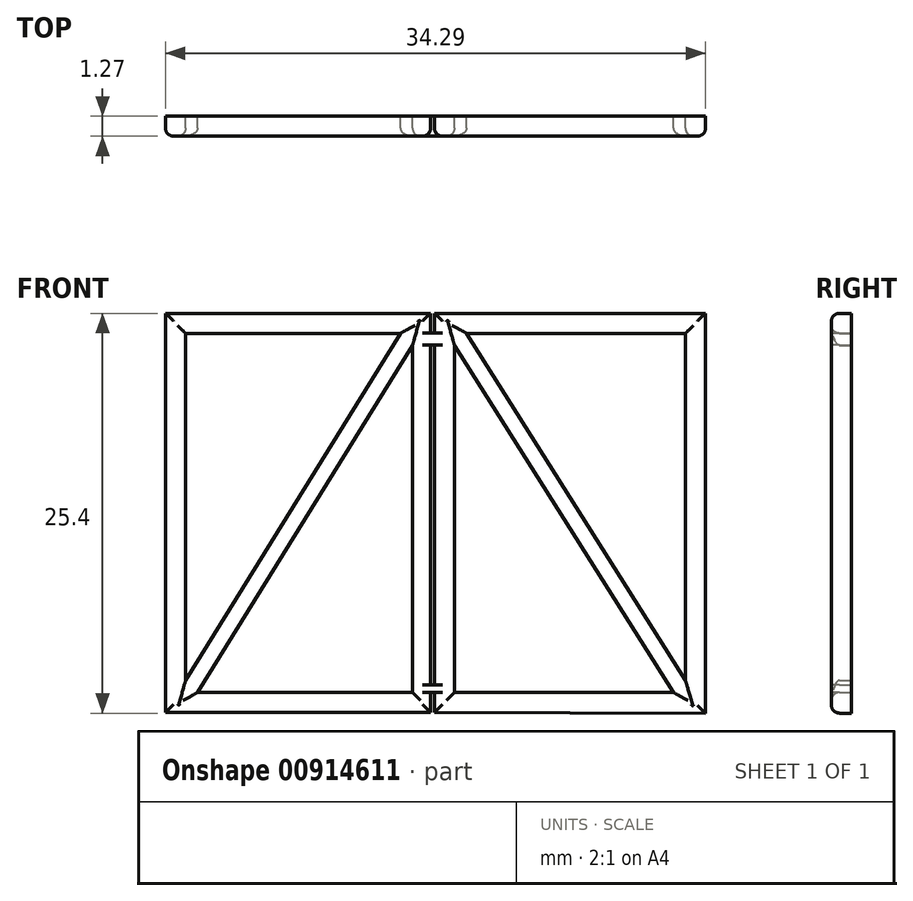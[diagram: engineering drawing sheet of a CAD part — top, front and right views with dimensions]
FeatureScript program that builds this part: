
annotation { "Feature Type Name" : "Feature", "Feature Type Description" : "" }
export const myFeature = defineFeature(function(context is Context, id is Id, definition is map)
    precondition{}
    {
        {
            var Q0;
            Q0=qCreatedBy(makeId("Front.planeOp"),FACE);
            var sketch = newSketch(context, id + "F0", { "sketchPlane" : qUnion([Q0])});
            skLineSegment(sketch, "E0", {"start": v(98.35, 38.1) * mm, "end": v(97.08, 38.1) * mm, "construction": true});
            skLineSegment(sketch, "E1", {"start": v(97.08, 38.1) * mm, "end": v(97.08, 35.56) * mm, "construction": true});
            skLineSegment(sketch, "E2", {"start": v(97.08, 35.56) * mm, "end": v(62.8, 35.56) * mm, "construction": true});
            skLineSegment(sketch, "E3", {"start": v(97.08, 7.62) * mm, "end": v(62.8, 7.62) * mm});
            skLineSegment(sketch, "E4", {"start": v(97.08, 8.9) * mm, "end": v(97.08, 34.3) * mm});
            skLineSegment(sketch, "E5", {"start": v(97.08, 0) * mm, "end": v(97.08, 6.35) * mm});
            skLineSegment(sketch, "E6", {"start": v(97.08, 6.35) * mm, "end": v(96.57, 6.35) * mm});
            skLineSegment(sketch, "E7", {"start": v(96.57, 6.35) * mm, "end": v(97.08, 6.91) * mm});
            skLineSegment(sketch, "E8", {"start": v(97.08, 6.91) * mm, "end": v(97.08, 7.62) * mm});
            skLineSegment(sketch, "E9.1.0.0", {"start": v(27.23, 8.9) * mm, "end": v(61.52, 8.9) * mm});
            skLineSegment(sketch, "E9.1.0.1", {"start": v(61.52, 7.62) * mm, "end": v(27.23, 7.62) * mm});
            skLineSegment(sketch, "E9.1.0.3", {"start": v(61.52, 0) * mm, "end": v(61.52, 6.35) * mm});
            skLineSegment(sketch, "E9.1.0.5", {"start": v(61.52, 8.9) * mm, "end": v(61.52, 34.3) * mm, "construction": true});
            skLineSegment(sketch, "E9.1.0.6", {"start": v(61.52, 35.56) * mm, "end": v(27.23, 35.56) * mm, "construction": true});
            skLineSegment(sketch, "E9.1.0.7", {"start": v(61.52, 38.1) * mm, "end": v(61.52, 35.56) * mm, "construction": true});
            skLineSegment(sketch, "E9.1.0.8", {"start": v(27.23, 34.3) * mm, "end": v(61.52, 34.3) * mm, "construction": true});
            skLineSegment(sketch, "E9.1.0.9", {"start": v(61.52, 6.35) * mm, "end": v(61.01, 6.35) * mm});
            skLineSegment(sketch, "E9.1.0.10", {"start": v(61.01, 6.35) * mm, "end": v(61.52, 6.91) * mm});
            skLineSegment(sketch, "E9.1.0.11", {"start": v(62.8, 38.1) * mm, "end": v(61.52, 38.1) * mm, "construction": true});
            skLineSegment(sketch, "E9.1.0.14", {"start": v(61.52, 6.91) * mm, "end": v(61.52, 7.62) * mm});
            skLineSegment(sketch, "E9.direction1", {"start": v(62.8, 7.62) * mm, "end": v(27.23, 7.62) * mm, "construction": true});
            skLineSegment(sketch, "E10", {"start": v(64.06, 10.22) * mm, "end": v(78.47, 10.22) * mm});
            skLineSegment(sketch, "E11", {"start": v(78.47, 33.02) * mm, "end": v(78.47, 10.22) * mm});
            skLineSegment(sketch, "E12", {"start": v(62.8, 8.95) * mm, "end": v(62.8, 34.3) * mm});
            skLineSegment(sketch, "E13", {"start": v(64.06, 10.22) * mm, "end": v(64.06, 33.02) * mm});
            skLineSegment(sketch, "E14", {"start": v(64.06, 33.02) * mm, "end": v(78.47, 33.02) * mm});
            skLineSegment(sketch, "E15", {"start": v(64.06, 10.22) * mm, "end": v(64.06, 10.98) * mm});
            skLineSegment(sketch, "E16", {"start": v(78.47, 33.02) * mm, "end": v(77.71, 33.02) * mm});
            skLineSegment(sketch, "E17", {"start": v(77.71, 33.02) * mm, "end": v(64.06, 10.98) * mm});
            skLineSegment(sketch, "E18", {"start": v(64.06, 10.22) * mm, "end": v(64.82, 10.22) * mm});
            skLineSegment(sketch, "E19", {"start": v(78.47, 33.02) * mm, "end": v(78.47, 32.26) * mm});
            skLineSegment(sketch, "E20", {"start": v(78.47, 32.26) * mm, "end": v(64.82, 10.22) * mm});
            skLineSegment(sketch, "E21", {"start": v(62.8, 8.95) * mm, "end": v(79.62, 8.95) * mm});
            skLineSegment(sketch, "E22", {"start": v(79.62, 34.3) * mm, "end": v(62.8, 34.3) * mm});
            skLineSegment(sketch, "E23", {"start": v(79.87, 8.95) * mm, "end": v(97.08, 8.9) * mm});
            skLineSegment(sketch, "E24", {"start": v(79.87, 34.3) * mm, "end": v(97.08, 34.3) * mm});
            skLineSegment(sketch, "E25", {"start": v(95.81, 33.02) * mm, "end": v(95.81, 10.22) * mm});
            skLineSegment(sketch, "E26", {"start": v(81.14, 10.22) * mm, "end": v(81.14, 33.02) * mm});
            skLineSegment(sketch, "E27", {"start": v(81.14, 33.02) * mm, "end": v(95.81, 33.02) * mm});
            skLineSegment(sketch, "E28", {"start": v(81.14, 10.22) * mm, "end": v(95.81, 10.22) * mm});
            skLineSegment(sketch, "E29", {"start": v(95.81, 10.22) * mm, "end": v(95.05, 10.22) * mm});
            skLineSegment(sketch, "E30", {"start": v(95.05, 10.22) * mm, "end": v(81.14, 32.26) * mm});
            skLineSegment(sketch, "E31", {"start": v(81.14, 33.02) * mm, "end": v(81.9, 33.02) * mm});
            skLineSegment(sketch, "E32", {"start": v(81.9, 33.02) * mm, "end": v(95.81, 10.98) * mm});
            skLineSegment(sketch, "E33", {"start": v(79.62, 33.03) * mm, "end": v(79.87, 33.03) * mm});
            skLineSegment(sketch, "E34", {"start": v(79.62, 32.27) * mm, "end": v(79.87, 32.27) * mm});
            skLineSegment(sketch, "E35", {"start": v(79.62, 10.22) * mm, "end": v(79.87, 10.22) * mm});
            skLineSegment(sketch, "E36", {"start": v(79.87, 10.7) * mm, "end": v(79.62, 10.7) * mm});
            skLineSegment(sketch, "E37", {"start": v(79.62, 10.22) * mm, "end": v(79.62, 8.95) * mm});
            skLineSegment(sketch, "E38", {"start": v(79.87, 10.22) * mm, "end": v(79.87, 8.95) * mm});
            skLineSegment(sketch, "E39", {"start": v(79.62, 10.7) * mm, "end": v(79.62, 32.27) * mm});
            skLineSegment(sketch, "E40", {"start": v(79.62, 33.03) * mm, "end": v(79.62, 34.3) * mm});
            skLineSegment(sketch, "E41", {"start": v(79.87, 34.3) * mm, "end": v(79.87, 33.03) * mm});
            skLineSegment(sketch, "E42", {"start": v(79.87, 32.27) * mm, "end": v(79.87, 10.7) * mm});
            skSolve(sketch);
        }
        {
            var Q0;
            Q0=makeQuery(id+"F0.imprint","IMPRINT",FACE,{"disambiguationData":[TD([[makeQuery(id+"F0.imprint","IMPRINT",EDGE,{"derivedFrom":sQuery(id+"F0.wireOp",EDGE,"E4")}),1.0]])]});
            var Q1;
            {var subQ3=sQuery(id+"F0.wireOp",EDGE,"E17");Q1=makeQuery(id+"F0.imprint","IMPRINT",FACE,{"disambiguationData":[TD([[makeQuery(id+"F0.imprint","IMPRINT",EDGE,{"derivedFrom":subQ3}),1.0]])]});}
            var Q2;
            {var subQ3=sQuery(id+"F0.wireOp",EDGE,"E30");Q2=makeQuery(id+"F0.imprint","IMPRINT",FACE,{"disambiguationData":[TD([[makeQuery(id+"F0.imprint","IMPRINT",EDGE,{"derivedFrom":subQ3}),-1.0]])]});}
            extrude(context, id + "F1", {"entities" : qUnion([Q0, Q1, Q2]), "depth" : 1.27 * mm, "offsetDistance" : 25.4 * mm});
        }
        {
            var Q0;
            Q0=makeQuery(id+"F1.opExtrude","CAP_EDGE",EDGE,{"disambiguationData":[OSD([sQuery(id+"F0.wireOp",EDGE,"E22")])],"isStart":false});
            var Q1;
            Q1=makeQuery(id+"F1.opExtrude","CAP_EDGE",EDGE,{"disambiguationData":[OSD([sQuery(id+"F0.wireOp",EDGE,"E14")])],"isStart":false});
            var Q2;
            Q2=makeQuery(id+"F1.opExtrude","CAP_EDGE",EDGE,{"disambiguationData":[OSD([sQuery(id+"F0.wireOp",EDGE,"E17")])],"isStart":false});
            var Q3;
            Q3=makeQuery(id+"F1.opExtrude","CAP_EDGE",EDGE,{"disambiguationData":[OSD([sQuery(id+"F0.wireOp",EDGE,"E20")])],"isStart":false});
            var Q4;
            Q4=makeQuery(id+"F1.opExtrude","CAP_EDGE",EDGE,{"disambiguationData":[OSD([sQuery(id+"F0.wireOp",EDGE,"E11")])],"isStart":false});
            var Q5;
            Q5=makeQuery(id+"F1.opExtrude","CAP_EDGE",EDGE,{"disambiguationData":[OSD([sQuery(id+"F0.wireOp",EDGE,"E39")])],"isStart":false});
            var Q6;
            Q6=makeQuery(id+"F1.opExtrude","CAP_EDGE",EDGE,{"disambiguationData":[OSD([sQuery(id+"F0.wireOp",EDGE,"E40")])],"isStart":false});
            var Q7;
            Q7=makeQuery(id+"F1.opExtrude","CAP_EDGE",EDGE,{"disambiguationData":[OSD([sQuery(id+"F0.wireOp",EDGE,"E41")])],"isStart":false});
            var Q8;
            Q8=makeQuery(id+"F1.opExtrude","CAP_EDGE",EDGE,{"disambiguationData":[OSD([sQuery(id+"F0.wireOp",EDGE,"E24")])],"isStart":false});
            var Q9;
            Q9=makeQuery(id+"F1.opExtrude","CAP_EDGE",EDGE,{"disambiguationData":[OSD([sQuery(id+"F0.wireOp",EDGE,"E26")])],"isStart":false});
            var Q10;
            Q10=makeQuery(id+"F1.opExtrude","CAP_EDGE",EDGE,{"disambiguationData":[OSD([sQuery(id+"F0.wireOp",EDGE,"E30")])],"isStart":false});
            var Q11;
            Q11=makeQuery(id+"F1.opExtrude","CAP_EDGE",EDGE,{"disambiguationData":[OSD([sQuery(id+"F0.wireOp",EDGE,"E27")])],"isStart":false});
            var Q12;
            Q12=makeQuery(id+"F1.opExtrude","CAP_EDGE",EDGE,{"disambiguationData":[OSD([sQuery(id+"F0.wireOp",EDGE,"E4")])],"isStart":false});
            var Q13;
            Q13=makeQuery(id+"F1.opExtrude","CAP_EDGE",EDGE,{"disambiguationData":[OSD([sQuery(id+"F0.wireOp",EDGE,"E25")])],"isStart":false});
            var Q14;
            Q14=makeQuery(id+"F1.opExtrude","CAP_EDGE",EDGE,{"disambiguationData":[OSD([sQuery(id+"F0.wireOp",EDGE,"E32")])],"isStart":false});
            var Q15;
            Q15=makeQuery(id+"F1.opExtrude","CAP_EDGE",EDGE,{"disambiguationData":[OSD([sQuery(id+"F0.wireOp",EDGE,"E23")])],"isStart":false});
            var Q16;
            Q16=makeQuery(id+"F1.opExtrude","CAP_EDGE",EDGE,{"disambiguationData":[OSD([sQuery(id+"F0.wireOp",EDGE,"E28")])],"isStart":false});
            var Q17;
            Q17=makeQuery(id+"F1.opExtrude","CAP_EDGE",EDGE,{"disambiguationData":[OSD([sQuery(id+"F0.wireOp",EDGE,"E42")])],"isStart":false});
            var Q18;
            Q18=makeQuery(id+"F1.opExtrude","CAP_EDGE",EDGE,{"disambiguationData":[OSD([sQuery(id+"F0.wireOp",EDGE,"E38")])],"isStart":false});
            var Q19;
            Q19=makeQuery(id+"F1.opExtrude","CAP_EDGE",EDGE,{"disambiguationData":[OSD([sQuery(id+"F0.wireOp",EDGE,"E37")])],"isStart":false});
            var Q20;
            Q20=makeQuery(id+"F1.opExtrude","CAP_EDGE",EDGE,{"disambiguationData":[OSD([sQuery(id+"F0.wireOp",EDGE,"E21")])],"isStart":false});
            var Q21;
            Q21=makeQuery(id+"F1.opExtrude","CAP_EDGE",EDGE,{"disambiguationData":[OSD([sQuery(id+"F0.wireOp",EDGE,"E10")])],"isStart":false});
            var Q22;
            Q22=makeQuery(id+"F1.opExtrude","CAP_EDGE",EDGE,{"disambiguationData":[OSD([sQuery(id+"F0.wireOp",EDGE,"E13")])],"isStart":false});
            var Q23;
            Q23=makeQuery(id+"F1.opExtrude","CAP_EDGE",EDGE,{"disambiguationData":[OSD([sQuery(id+"F0.wireOp",EDGE,"E12")])],"isStart":false});
            fillet(context, id + "F2", {"entities" : qUnion([Q0, Q1, Q2, Q3, Q4, Q5, Q6, Q7, Q8, Q9, Q10, Q11, Q12, Q13, Q14, Q15, Q16, Q17, Q18, Q19, Q20, Q21, Q22, Q23]), "radius" : 0.5 * mm, "tangentPropagation" : true, "allowEdgeOverflow" : false});
        }
    });
